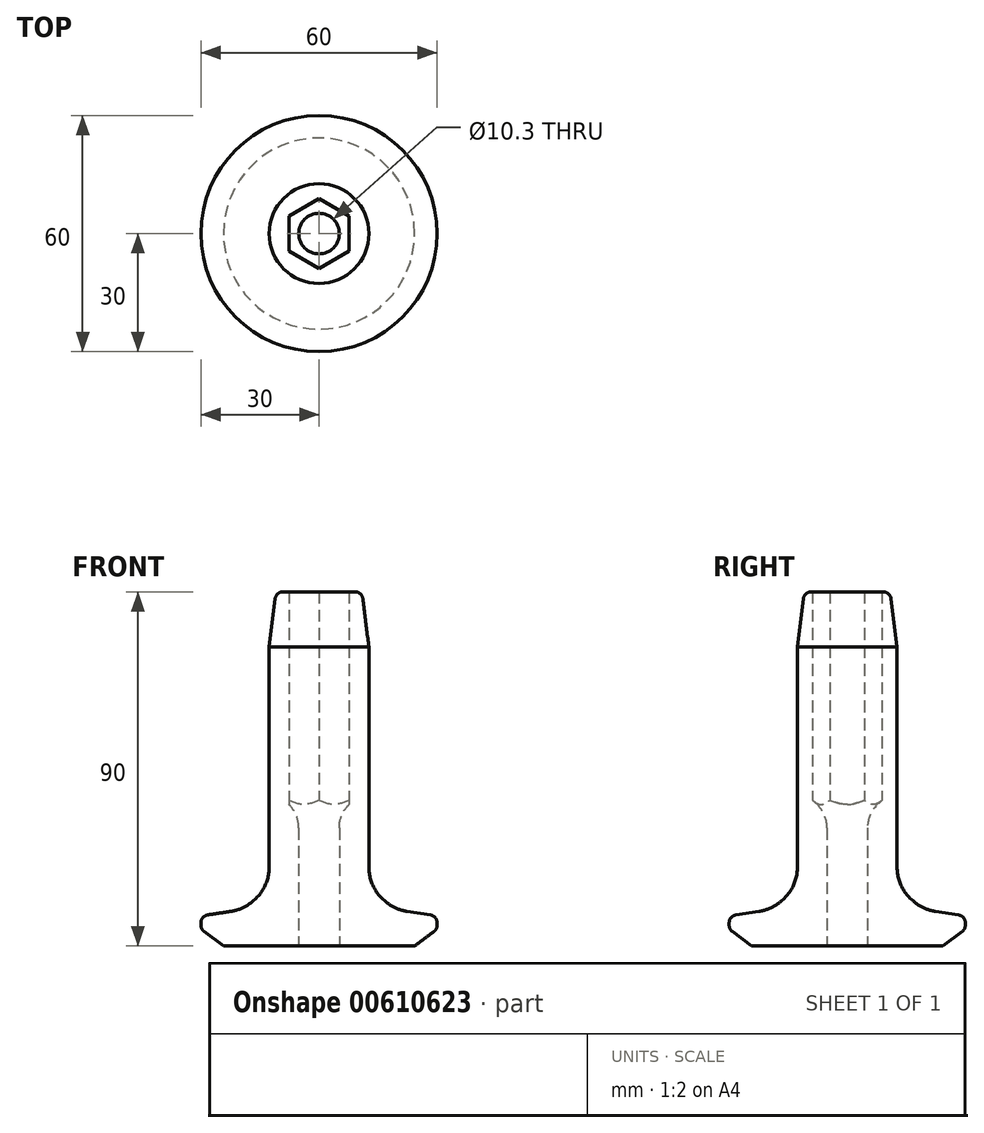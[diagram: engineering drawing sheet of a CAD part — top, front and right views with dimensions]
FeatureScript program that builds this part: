
annotation { "Feature Type Name" : "Feature", "Feature Type Description" : "" }
export const myFeature = defineFeature(function(context is Context, id is Id, definition is map)
    precondition{}
    {
        {
            var Q0;
            Q0=qCreatedBy(makeId("Top.planeOp"),FACE);
            var sketch = newSketch(context, id + "F0", { "sketchPlane" : qUnion([Q0])});
            skCircle(sketch, "E0", {"center": v(0, 0) * mm, "radius": 5 * mm});
            skSolve(sketch);
        }
        {
            var Q0;
            Q0=makeQuery(id+"F0.imprint","IMPRINT",FACE,{"disambiguationData":[TD([[makeQuery(id+"F0.imprint","IMPRINT",EDGE,{"derivedFrom":sQuery(id+"F0.wireOp",EDGE,"E0")}),1.0]])]});
            extrude(context, id + "F1", {"entities" : qUnion([Q0]), "depth" : 37 * mm, "offsetDistance" : 25 * mm});
        }
        {
            var Q0;
            Q0=makeQuery(id+"F1.opExtrude","CAP_FACE",FACE,{"disambiguationData":[OSD([sQuery(id+"F0.wireOp",EDGE,"E0")])],"isStart":false});
            var sketch = newSketch(context, id + "F2", { "sketchPlane" : qUnion([Q0])});
            skCircle(sketch, "E1.cCircle", {"center": v(0, 0) * mm, "radius": 7.5 * mm, "construction": true});
            skLineSegment(sketch, "E1.0", {"start": v(-7.5, -4.33) * mm, "end": v(-7.5, 4.33) * mm});
            skLineSegment(sketch, "E1.1", {"start": v(-7.5, 4.33) * mm, "end": v(0, 8.66) * mm});
            skLineSegment(sketch, "E1.2", {"start": v(0, 8.66) * mm, "end": v(7.5, 4.33) * mm});
            skLineSegment(sketch, "E1.3", {"start": v(7.5, 4.33) * mm, "end": v(7.5, -4.33) * mm});
            skLineSegment(sketch, "E1.4", {"start": v(7.5, -4.33) * mm, "end": v(0, -8.66) * mm});
            skLineSegment(sketch, "E1.5", {"start": v(0, -8.66) * mm, "end": v(-7.5, -4.33) * mm});
            skPoint(sketch, "E1.0.midPoint", {"position": v(-7.5, 0) * mm});
            skSolve(sketch);
        }
        {
            var Q0;
            Q0=makeQuery(id+"F2.imprint","IMPRINT",FACE,{"disambiguationData":[TD([[makeQuery(id+"F2.imprint","IMPRINT",EDGE,{"derivedFrom":sQuery(id+"F2.wireOp",EDGE,"E1.0")}),-1.0]])]});
            var Q1;
            Q1=makeQuery(id+"F2.imprint","IMPRINT",FACE,{"disambiguationData":[TD([[makeQuery(id+"F2.imprint","IMPRINT",EDGE,{"derivedFrom":makeQuery(id+"F1.opExtrude","CAP_EDGE",EDGE,{"disambiguationData":[OSD([sQuery(id+"F0.wireOp",EDGE,"E0")])],"isStart":false})}),1.0]])]});
            extrude(context, id + "F3", {"entities" : qUnion([Q0, Q1]), "operationType" : NewBodyOperationType.ADD, "depth" : 50 * mm, "offsetDistance" : 25 * mm});
        }
        {
            var Q0;
            Q0=qCreatedBy(makeId("Right.planeOp"),FACE);
            var sketch = newSketch(context, id + "F4", { "sketchPlane" : qUnion([Q0])});
            skArc(sketch, "E2", {"start": v(-5, 37) * mm, "mid": v(-5.97, 40.95) * mm, "end": v(-8.66, 44) * mm});
            skLineSegment(sketch, "E3", {"start": v(-5, 37) * mm, "end": v(-5, 22.17) * mm});
            skLineSegment(sketch, "E4", {"start": v(-8.66, 44) * mm, "end": v(-8.66, 25.2) * mm});
            skLineSegment(sketch, "E5", {"start": v(-8.66, 25.2) * mm, "end": v(-5, 22.17) * mm});
            skSolve(sketch);
        }
        {
            var Q0;
            Q0=makeQuery(id+"F4.imprint","IMPRINT",FACE,{"disambiguationData":[TD([[makeQuery(id+"F4.imprint","IMPRINT",EDGE,{"derivedFrom":sQuery(id+"F4.wireOp",EDGE,"E2")}),1.0]])]});
            var Q1;
            Q1=makeQuery(id+"F1.opExtrude","SWEPT_FACE",FACE,{"disambiguationData":[OSD([sQuery(id+"F0.wireOp",EDGE,"E0")])]});
            revolve(context, id + "F5", {"operationType" : NewBodyOperationType.REMOVE, "entities" : qUnion([Q0]), "axis" : qUnion([Q1]), "revolveType" : RevolveType.FULL, "oppositeDirection" : true});
        }
        {
            var Q0;
            Q0=qCreatedBy(makeId("Top.planeOp"),FACE);
            cPlane(context, id + "F6", {"entities" : qUnion([Q0]), "cplaneType" : CPlaneType.OFFSET, "offset" : (44 - 37) * mm, "width" : 150 * mm, "height" : 150 * mm});
        }
        {
            var Q0;
            Q0=qCreatedBy(makeId("Right.planeOp"),FACE);
            var sketch = newSketch(context, id + "F7", { "sketchPlane" : qUnion([Q0])});
            skLineSegment(sketch, "E6", {"start": v(0, 7) * mm, "end": v(24.29, 7) * mm});
            skLineSegment(sketch, "E7", {"start": v(24.29, 7) * mm, "end": v(30, 11.26) * mm});
            skLineSegment(sketch, "E8", {"start": v(30, 11.26) * mm, "end": v(30, 14.64) * mm});
            skLineSegment(sketch, "E9", {"start": v(30, 14.64) * mm, "end": v(19.1, 16.27) * mm});
            skLineSegment(sketch, "E10", {"start": v(19.1, 16.27) * mm, "end": v(12.66, 22.15) * mm});
            skLineSegment(sketch, "E11", {"start": v(12.66, 22.15) * mm, "end": v(12.66, 83) * mm});
            skLineSegment(sketch, "E12", {"start": v(12.66, 83) * mm, "end": v(10.91, 97) * mm});
            skLineSegment(sketch, "E13", {"start": v(10.91, 97) * mm, "end": v(0, 97) * mm});
            skLineSegment(sketch, "E14", {"start": v(0, 97) * mm, "end": v(0, 7) * mm});
            skSolve(sketch);
        }
        {
            var Q0;
            Q0=makeQuery(id+"F3.opExtrude","CAP_FACE",FACE,{"disambiguationData":[OSD([sQuery(id+"F2.wireOp",EDGE,"E1.0"),sQuery(id+"F2.wireOp",EDGE,"E1.1"),sQuery(id+"F2.wireOp",EDGE,"E1.2"),sQuery(id+"F2.wireOp",EDGE,"E1.3"),sQuery(id+"F2.wireOp",EDGE,"E1.4"),sQuery(id+"F2.wireOp",EDGE,"E1.5")])],"isStart":false});
            extrude(context, id + "F8", {"entities" : qUnion([Q0]), "operationType" : NewBodyOperationType.ADD, "depth" : 25 * mm, "offsetDistance" : 25 * mm});
        }
        {
            var Q0;
            Q0=makeQuery(id+"F7.imprint","IMPRINT",FACE,{"disambiguationData":[TD([[makeQuery(id+"F7.imprint","IMPRINT",EDGE,{"derivedFrom":sQuery(id+"F7.wireOp",EDGE,"E6")}),1.0]])]});
            var Q1;
            Q1=sQuery(id+"F7.wireOp",EDGE,"E14");
            revolve(context, id + "F9", {"entities" : qUnion([Q0]), "axis" : qUnion([Q1]), "revolveType" : RevolveType.FULL});
        }
        {
            var Q0;
            Q0=makeQuery(id+"F9.opRevolve","SWEPT_EDGE",EDGE,{"disambiguationData":[OSD([sQuery(id+"F7.wireOp",EDGE,"E9"),sQuery(id+"F7.wireOp",EDGE,"E10")])]});
            var Q1;
            Q1=makeQuery(id+"F9.opRevolve","SWEPT_EDGE",EDGE,{"disambiguationData":[OSD([sQuery(id+"F7.wireOp",EDGE,"E10"),sQuery(id+"F7.wireOp",EDGE,"E11")])]});
            fillet(context, id + "F10", {"entities" : qUnion([Q0, Q1]), "radius" : 11 * mm, "tangentPropagation" : true, "allowEdgeOverflow" : false});
        }
        {
            var Q0;
            Q0=makeQuery(id+"F9.opRevolve","SWEPT_EDGE",EDGE,{"disambiguationData":[OSD([sQuery(id+"F7.wireOp",EDGE,"E8"),sQuery(id+"F7.wireOp",EDGE,"E9")])]});
            var Q1;
            Q1=makeQuery(id+"F9.opRevolve","SWEPT_EDGE",EDGE,{"disambiguationData":[OSD([sQuery(id+"F7.wireOp",EDGE,"E7"),sQuery(id+"F7.wireOp",EDGE,"E8")])]});
            var Q2;
            Q2=makeQuery(id+"F9.opRevolve","SWEPT_EDGE",EDGE,{"disambiguationData":[OSD([sQuery(id+"F7.wireOp",EDGE,"E12"),sQuery(id+"F7.wireOp",EDGE,"E13")])]});
            fillet(context, id + "F11", {"entities" : qUnion([Q0, Q1, Q2]), "radius" : 2 * mm, "tangentPropagation" : true, "allowEdgeOverflow" : false});
        }
        {
            var Q0;
            Q0=makeQuery(id+"F1.opExtrude","SWEPT_BODY",BODY,{"disambiguationData":[OSD([sQuery(id+"F0.wireOp",EDGE,"E0")])]});
            var Q1;
            Q1=makeQuery(id+"F9.opRevolve","SWEPT_BODY",BODY,{"disambiguationData":[OSD([sQuery(id+"F7.wireOp",EDGE,"E6"),sQuery(id+"F7.wireOp",EDGE,"E7"),sQuery(id+"F7.wireOp",EDGE,"E8"),sQuery(id+"F7.wireOp",EDGE,"E9"),sQuery(id+"F7.wireOp",EDGE,"E10"),sQuery(id+"F7.wireOp",EDGE,"E11"),sQuery(id+"F7.wireOp",EDGE,"E12"),sQuery(id+"F7.wireOp",EDGE,"E13"),sQuery(id+"F7.wireOp",EDGE,"E14")])]});
            booleanBodies(context, id + "F12", {"operationType" : BooleanOperationType.SUBTRACTION, "tools" : qUnion([Q0]), "targets" : qUnion([Q1]), "offset" : true, "offsetAll" : true, "offsetDistance" : .15 * mm});
        }
    });
